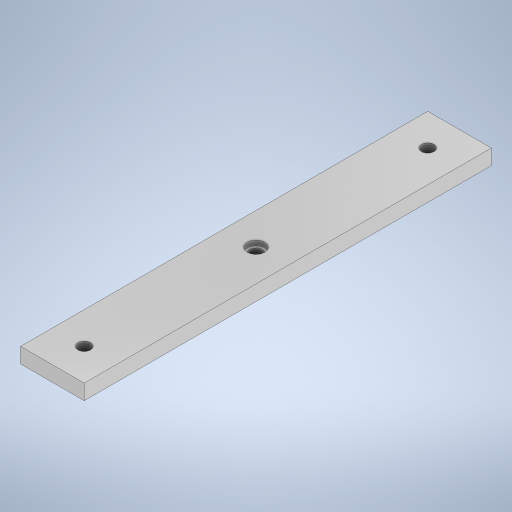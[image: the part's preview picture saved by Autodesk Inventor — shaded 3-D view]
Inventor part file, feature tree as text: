
AUTODESK INVENTOR PART (.ipt)
format: ipt  version: 2023 (Build 270158000, 158)  size: 276,480 bytes
history: native  units: mm
features: sketch x3, hole x2, thread x2, extrude x1
ambient origin geometry x8: Origin, YZ Plane, XZ Plane, XY Plane, X Axis, Y Axis, Z Axis, Center Point
bodies: Solid1 (feature_tree)
feature tree (8):
  extrude  "Extrusion1"  Depth=160.0mm
  hole  "Hole1"  [1 undecoded]
  hole  "Furo2"  [1 undecoded]
  thread  "Rosca1"  [1 undecoded]
  thread  "Rosca2"  [1 undecoded]
  sketch  "Sketch1"  dims[d0=25.0mm d1=160.0mm]
  sketch  "Sketch2"  dims[d2=6.0mm d3=0.0mm d4=25.0mm]
  sketch  "Esboço3"  dims[d5=160.0mm d6=12.5mm d7=12.5mm d8=12.5mm d9=12.5mm d10=5.0mm d11=6.0mm d12=4.0mm d13=2.0mm d14=90.0deg d15=0.5mm d16=20.594885mm d17=160.0mm d18=25.0mm d19=12.5mm d20=80.0mm d21=5.0mm d22=6.0mm d23=7.0mm d24=2.0mm d25=90.0deg d26=0.5mm d27=20.594885mm d28=43.6mm d29=0.0mm d30=15.0mm d31=0.0mm]
note: 4 required parameter values undecoded (feature->parameter linkage not recoverable at this tier; creation-order binding heuristic only, values carry confidence <= 0.55)
